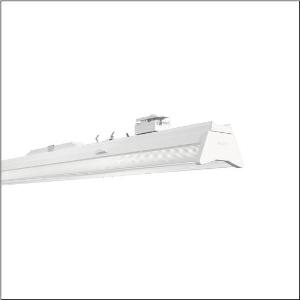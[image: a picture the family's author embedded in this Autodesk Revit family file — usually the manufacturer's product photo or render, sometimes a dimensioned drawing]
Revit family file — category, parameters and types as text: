
# Revit family: licross_r__21_performance_mo_52td16dn445g_3218
name_source: partatom
category: Lighting Fixtures
units: mm (PartAtom-declared; Revit-internal decimal feet)

## family parameters
Cut with Voids When Loaded = No
Host = Face
Light Source = No
Part Type = Normal
Room Calculation Point = No
Round Connector Dimension = Use Diameter
Shared = No

## types (1)
- --- (1 x LED, 4500 lm, 24.9 W, 4000K)
    Apparent Load = 25 VA
    CIE Flux Codes = 66 88 96 79 100
    Color Rendering = 80
    Color Temperature = 4000K
    Default Elevation = 1800 mm
    Description = Licross® 21 Performance MO, luminaire insert, of sheet steel, galvanised, coil coated, white, length: 1.500mm, width: 120mm, height: 123mm, LED rated luminous flux: 4.500lm, light colour: 840, control gear: DALI 2, with plug, 5-pole, with phase selection, mains connection: 220..240V, AC, 50/60Hz, rated input power: 25W, halogen-free wiring, primary light control with lens, of plastic, primary optical cover: cover, of PMMA, CAT 2 (L<= 3000cd/m²), light emission: direct/indirect distribution, primary light characteristic: symmetric, protection rating (complete): IP54, insulation class (complete): insulation class I (protective earthing), certification: CE, ENEC, VDE, UKCA, protection symbol: D if used in an environment with non-conductive dust loads with corresponding accessories, impact resistance: IK06, permissible ambient temperature for indoor applications: -25..+50°C, corresponds to IFS (International Featured Standards) requirements for safety and quality in the food industry, reducing of maximum allowable ambient temperature of 5°C with ceiling mounting, LABS conformity tested according to VDMA 24364:2018-05, packaging unit: 1 piece
    Height = 114 mm
    Lamp = 1 x LED
    Lamp Light Flux = 4500 lm
    Lamp Power = 24.9 W
    Lamp count = 1
    Length = 1500 mm
    Luminous efficacy = 181 lm/W
    Manufacturer = Siteco
    ModVariant = No
    Model = 52TD16DN445G
    Mounting Place = Ceiling
    Mounting Type = Pendant
    Number of Poles = 1
    OnlyDefault = Yes
    Power Factor = 1
    Product Name = Licross® 21 Performance MO
    Product group = luminaire insert
    ProductGroupID = 901
    Protection Class = Protection class I
    Protection Degree = IP 54
    RLX_Detail_Level = 1
    RLX_Emergency_Light_Flux = 0 lm
    RLX_Emergency_Type = 0
    RLX_Emergency_Type_DB = No
    RlxData = <blob elided: 33529 chars, md5=03fdfc8d>
    Socket = socket
    Standby Power = 0 W
    System Light Flux = 4500 lm
    System Power = 25 W
    Type Comments = factory setting: luminous flux: 100 % | dim-lin: 254 | 165 mA
    Type Image = l_1256138.jpg
    URL = http://relux.com
    VarID = @adj_015885
    Voltage = 0 V
    Weight = 0.00 kg
    Width = 120 mm

## geometry (parser evidence)
native form markers: Blend x4, Sweep x14
no freeform markers — native parametric forms only
